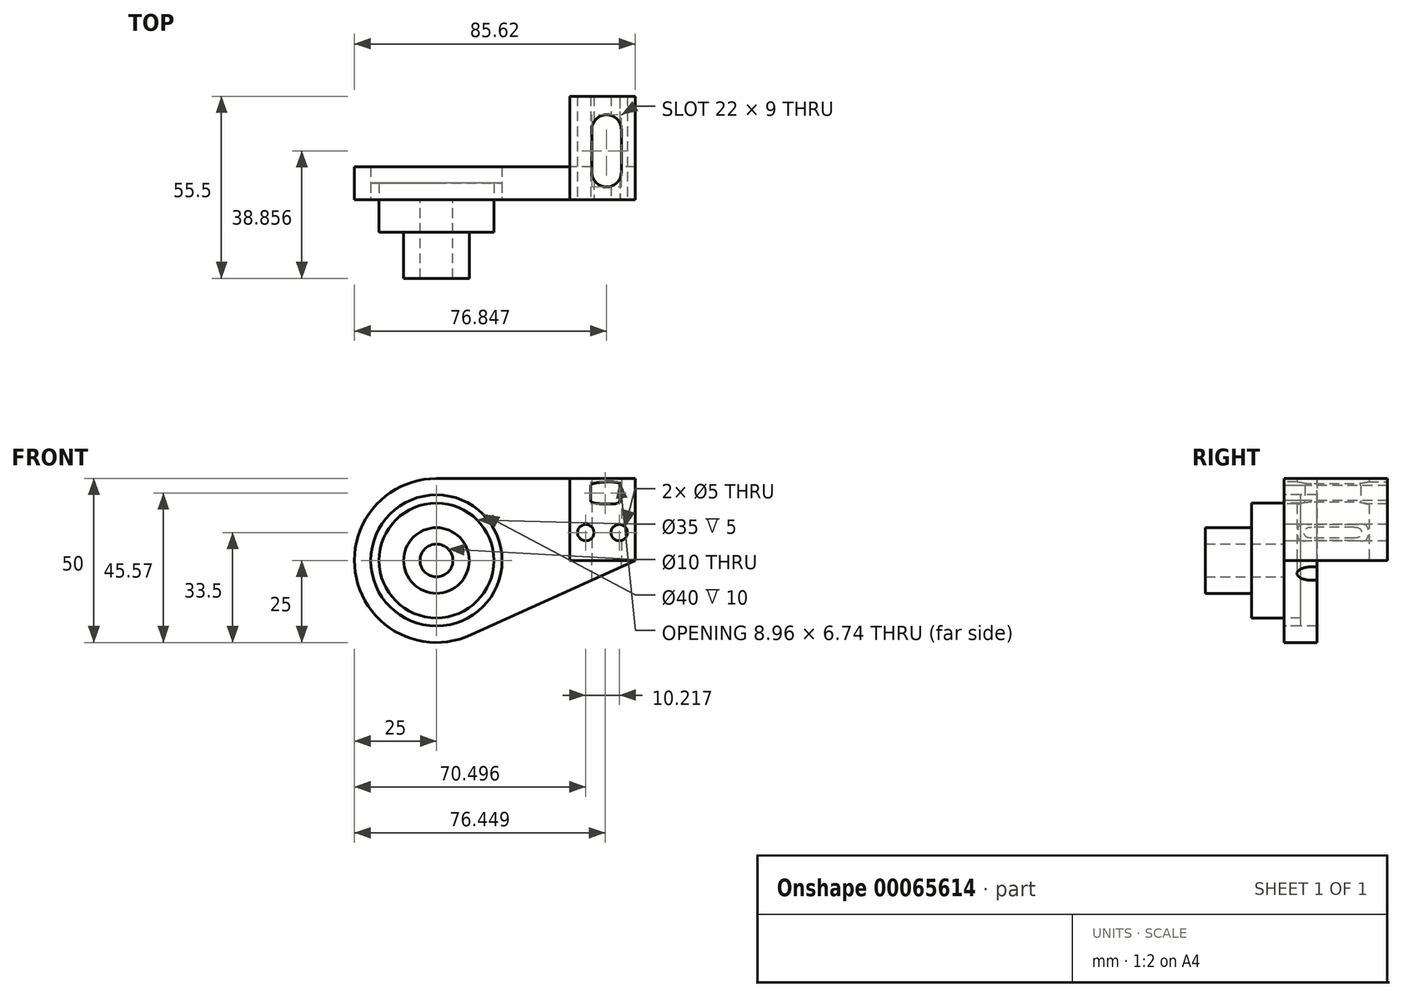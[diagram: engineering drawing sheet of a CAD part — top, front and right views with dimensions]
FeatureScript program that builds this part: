
annotation { "Feature Type Name" : "Feature", "Feature Type Description" : "" }
export const myFeature = defineFeature(function(context is Context, id is Id, definition is map)
    precondition{}
    {
        {
            var Q0;
            Q0=qCreatedBy(makeId("Front.planeOp"),FACE);
            var sketch = newSketch(context, id + "F0", { "sketchPlane" : qUnion([Q0])});
            skCircle(sketch, "E0", {"center": v(0, 0) * mm, "radius": 5 * mm});
            skCircle(sketch, "E1", {"center": v(0, 0) * mm, "radius": 10 * mm});
            skCircle(sketch, "E2", {"center": v(0, 0) * mm, "radius": 17.5 * mm});
            skCircle(sketch, "E3", {"center": v(0, 0) * mm, "radius": 20 * mm});
            skLineSegment(sketch, "E4", {"start": v(10.51, -22.68) * mm, "end": v(60.62, 0) * mm});
            skLineSegment(sketch, "E5", {"start": v(60.62, 0) * mm, "end": v(60.62, 25) * mm});
            skLineSegment(sketch, "E6", {"start": v(0, 25) * mm, "end": v(40.62, 25) * mm});
            skLineSegment(sketch, "E7", {"start": v(40.62, 25) * mm, "end": v(60.62, 25) * mm});
            skLineSegment(sketch, "E8", {"start": v(60.62, 0) * mm, "end": v(40.62, 0) * mm});
            skLineSegment(sketch, "E9", {"start": v(40.62, 0) * mm, "end": v(40.62, 25) * mm});
            skLineSegment(sketch, "E10", {"start": v(60.62, 17) * mm, "end": v(40.62, 17) * mm});
            skArc(sketch, "E11", {"start": v(0, 25) * mm, "mid": v(-24.41, -5.38) * mm, "end": v(10.51, -22.68) * mm});
            skCircle(sketch, "E12", {"center": v(45.5, 8.5) * mm, "radius": 2.5 * mm});
            skCircle(sketch, "E13", {"center": v(55.71, 8.5) * mm, "radius": 2.5 * mm});
            skLineSegment(sketch, "E14", {"start": v(46.97, 22.8) * mm, "end": v(46.97, 18.25) * mm});
            skLineSegment(sketch, "E15", {"start": v(55.89, 22.8) * mm, "end": v(55.89, 18.25) * mm});
            skFitSpline(sketch, "E16", {"points": [v(46.97, 22.8) * mm, v(47.49, 23.37) * mm, v(55.68, 23.6) * mm, v(55.89, 22.8) * mm], "startDerivative": vector(0.65, 3.16) * mm, "endDerivative": vector(-1.26, -4.59) * mm});
            skFitSpline(sketch, "E17", {"points": [v(46.97, 18.25) * mm, v(47.49, 17.7) * mm, v(55.4, 17.52) * mm, v(55.89, 18.25) * mm], "startDerivative": vector(0.79, -3.1) * mm, "endDerivative": vector(0.3, 4) * mm});
            skSolve(sketch);
        }
        {
            var Q0;
            Q0=makeQuery(id+"F0.imprint","IMPRINT",FACE,{"disambiguationData":[TD([[makeQuery(id+"F0.imprint","IMPRINT",EDGE,{"derivedFrom":sQuery(id+"F0.wireOp",EDGE,"E3")}),-1.0]])]});
            extrude(context, id + "F1", {"entities" : qUnion([Q0]), "oppositeDirection" : true, "depth" : 10 * mm});
        }
        {
            var Q0;
            Q0=makeQuery(id+"F0.imprint","IMPRINT",FACE,{"disambiguationData":[TD([[makeQuery(id+"F0.imprint","IMPRINT",EDGE,{"derivedFrom":sQuery(id+"F0.wireOp",EDGE,"E2")}),-1.0]])]});
            extrude(context, id + "F2", {"entities" : qUnion([Q0]), "oppositeDirection" : true, "depth" : 5 * mm});
        }
        {
            var Q0;
            Q0=makeQuery(id+"F0.imprint","IMPRINT",FACE,{"disambiguationData":[TD([[makeQuery(id+"F0.imprint","IMPRINT",EDGE,{"derivedFrom":sQuery(id+"F0.wireOp",EDGE,"E1")}),-1.0]])]});
            extrude(context, id + "F3", {"entities" : qUnion([Q0]), "depth" : 10 * mm});
        }
        {
            var Q0;
            Q0=makeQuery(id+"F0.imprint","IMPRINT",FACE,{"disambiguationData":[TD([[makeQuery(id+"F0.imprint","IMPRINT",EDGE,{"derivedFrom":sQuery(id+"F0.wireOp",EDGE,"E0")}),-1.0]])]});
            extrude(context, id + "F4", {"entities" : qUnion([Q0]), "operationType" : NewBodyOperationType.ADD, "depth" : 24 * mm});
        }
        {
            var Q0;
            {var subQ1=sQuery(id+"F0.wireOp",EDGE,"E8");Q0=makeQuery(id+"F0.imprint","IMPRINT",FACE,{"disambiguationData":[TD([[makeQuery(id+"F0.imprint","IMPRINT",EDGE,{"derivedFrom":subQ1}),-1.0]])]});}
            var Q1;
            {var subQ2=sQuery(id+"F0.wireOp",EDGE,"E7");Q1=makeQuery(id+"F0.imprint","IMPRINT",FACE,{"disambiguationData":[TD([[makeQuery(id+"F0.imprint","IMPRINT",EDGE,{"derivedFrom":subQ2}),-1.0]])]});}
            extrude(context, id + "F5", {"entities" : qUnion([Q0, Q1]), "oppositeDirection" : true, "depth" : 31.5 * mm});
        }
        {
            var Q0;
            Q0=qCreatedBy(makeId("Top.planeOp"),FACE);
            var sketch = newSketch(context, id + "F6", { "sketchPlane" : qUnion([Q0])});
            skLineSegment(sketch, "E18", {"start": v(47.35, 21.36) * mm, "end": v(47.35, 8.36) * mm});
            skLineSegment(sketch, "E19", {"start": v(56.35, 21.36) * mm, "end": v(56.35, 8.36) * mm});
            skArc(sketch, "E20", {"start": v(56.35, 21.36) * mm, "mid": v(51.85, 25.86) * mm, "end": v(47.35, 21.36) * mm});
            skArc(sketch, "E21", {"start": v(47.35, 8.36) * mm, "mid": v(51.85, 3.86) * mm, "end": v(56.35, 8.36) * mm});
            skSolve(sketch);
        }
        {
            var Q0;
            Q0 = qSketchRegion(id + "F6", true);
            extrude(context, id + "F7", {"entities" : qUnion([Q0]), "operationType" : NewBodyOperationType.REMOVE, "depth" : 25 * mm, "hasSecondDirection" : true, "secondDirectionOppositeDirection" : true, "secondDirectionDepth" : 25 * mm});
        }
    });
